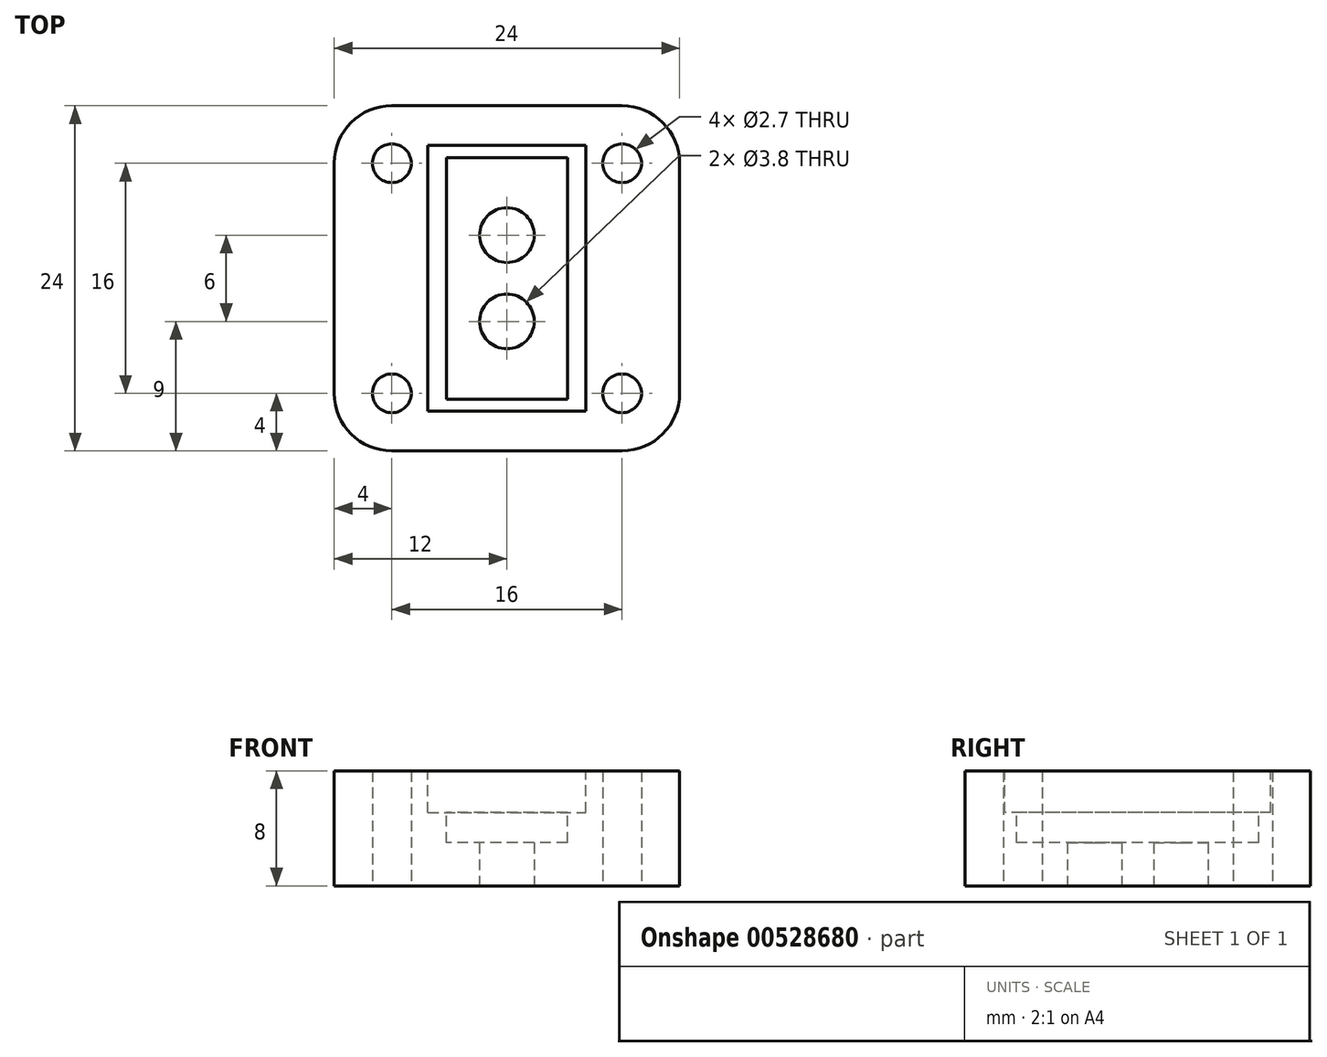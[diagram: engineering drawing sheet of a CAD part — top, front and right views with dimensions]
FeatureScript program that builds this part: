
annotation { "Feature Type Name" : "Feature", "Feature Type Description" : "" }
export const myFeature = defineFeature(function(context is Context, id is Id, definition is map)
    precondition{}
    {
        {
            var Q0;
            Q0=qCreatedBy(makeId("Top.planeOp"),FACE);
            var sketch = newSketch(context, id + "F0", { "sketchPlane" : qUnion([Q0])});
            skLineSegment(sketch, "E0.bottom", {"start": v(12, 12) * mm, "end": v(-12, 12) * mm});
            skLineSegment(sketch, "E0.top", {"start": v(12, -12) * mm, "end": v(-12, -12) * mm});
            skLineSegment(sketch, "E0.left", {"start": v(12, 12) * mm, "end": v(12, -12) * mm});
            skLineSegment(sketch, "E0.right", {"start": v(-12, 12) * mm, "end": v(-12, -12) * mm});
            skPoint(sketch, "E0.middle", {"position": v(0, 0) * mm});
            skLineSegment(sketch, "E1", {"start": v(0, 0) * mm, "end": v(-8, 0) * mm, "construction": true});
            skLineSegment(sketch, "E2", {"start": v(-8, 0) * mm, "end": v(-8, 8) * mm, "construction": true});
            skLineSegment(sketch, "E3", {"start": v(0, 0) * mm, "end": v(0, 3) * mm, "construction": true});
            skCircle(sketch, "E4", {"center": v(-8, 8) * mm, "radius": 1.35 * mm});
            skCircle(sketch, "E5", {"center": v(0, 3) * mm, "radius": 1.9 * mm});
            skCircle(sketch, "E6.0.1.0", {"center": v(-8, -8) * mm, "radius": 1.35 * mm});
            skCircle(sketch, "E6.1.0.0", {"center": v(8, 8) * mm, "radius": 1.35 * mm});
            skCircle(sketch, "E6.1.1.0", {"center": v(8, -8) * mm, "radius": 1.35 * mm});
            skLineSegment(sketch, "E6.direction1", {"start": v(-8, 8) * mm, "end": v(8, 8) * mm, "construction": true});
            skLineSegment(sketch, "E6.direction2", {"start": v(-8, 8) * mm, "end": v(-8, -8) * mm, "construction": true});
            skCircle(sketch, "E7.MirrorC", {"center": v(0, -3) * mm, "radius": 1.9 * mm});
            skSolve(sketch);
        }
        {
            var Q0;
            Q0=makeQuery(id+"F0.imprint","IMPRINT",FACE,{"disambiguationData":[TD([[makeQuery(id+"F0.imprint","IMPRINT",EDGE,{"derivedFrom":sQuery(id+"F0.wireOp",EDGE,"E0.bottom")}),1.0]])]});
            extrude(context, id + "F1", {"entities" : qUnion([Q0]), "depth" : 8 * mm, "offsetDistance" : 25 * mm});
        }
        {
            var Q0;
            Q0=makeQuery(id+"F1.opExtrude","CAP_FACE",FACE,{"disambiguationData":[OSD([sQuery(id+"F0.wireOp",EDGE,"E0.bottom"),sQuery(id+"F0.wireOp",EDGE,"E0.top"),sQuery(id+"F0.wireOp",EDGE,"E0.left"),sQuery(id+"F0.wireOp",EDGE,"E0.right"),sQuery(id+"F0.wireOp",EDGE,"E4"),sQuery(id+"F0.wireOp",EDGE,"E5"),sQuery(id+"F0.wireOp",EDGE,"E6.0.1.0"),sQuery(id+"F0.wireOp",EDGE,"E6.1.0.0"),sQuery(id+"F0.wireOp",EDGE,"E6.1.1.0"),sQuery(id+"F0.wireOp",EDGE,"E7.MirrorC")])],"isStart":false});
            var sketch = newSketch(context, id + "F2", { "sketchPlane" : qUnion([Q0])});
            skLineSegment(sketch, "E8.bottom", {"start": v(4.2, 8.4) * mm, "end": v(-4.2, 8.4) * mm});
            skLineSegment(sketch, "E8.top", {"start": v(4.2, -8.4) * mm, "end": v(-4.2, -8.4) * mm});
            skLineSegment(sketch, "E8.left", {"start": v(4.2, 8.4) * mm, "end": v(4.2, -8.4) * mm});
            skLineSegment(sketch, "E8.right", {"start": v(-4.2, 8.4) * mm, "end": v(-4.2, -8.4) * mm});
            skPoint(sketch, "E8.middle", {"position": v(0, 0) * mm});
            skLineSegment(sketch, "E9", {"start": v(-8, 8) * mm, "end": v(-8, 0) * mm, "construction": true});
            skCircle(sketch, "E10", {"center": v(0, 0) * mm, "radius": 8 * mm, "construction": true});
            skLineSegment(sketch, "E11.bottom", {"start": v(-9.25, 9.25) * mm, "end": v(9.25, 9.25) * mm, "construction": true});
            skLineSegment(sketch, "E11.top", {"start": v(-9.25, -9.25) * mm, "end": v(9.25, -9.25) * mm, "construction": true});
            skLineSegment(sketch, "E11.left", {"start": v(-9.25, 9.25) * mm, "end": v(-9.25, -9.25) * mm, "construction": true});
            skLineSegment(sketch, "E11.right", {"start": v(9.25, 9.25) * mm, "end": v(9.25, -9.25) * mm, "construction": true});
            skLineSegment(sketch, "E12.bottom", {"start": v(-5.5, 9.25) * mm, "end": v(5.5, 9.25) * mm});
            skLineSegment(sketch, "E12.top", {"start": v(-5.5, -9.25) * mm, "end": v(5.5, -9.25) * mm});
            skLineSegment(sketch, "E12.left", {"start": v(-5.5, 9.25) * mm, "end": v(-5.5, -9.25) * mm});
            skLineSegment(sketch, "E12.right", {"start": v(5.5, 9.25) * mm, "end": v(5.5, -9.25) * mm});
            skSolve(sketch);
        }
        {
            var Q0;
            Q0=makeQuery(id+"F2.imprint","IMPRINT",FACE,{"disambiguationData":[TD([[makeQuery(id+"F2.imprint","IMPRINT",EDGE,{"derivedFrom":sQuery(id+"F2.wireOp",EDGE,"E8.bottom")}),1.0]])]});
            extrude(context, id + "F3", {"entities" : qUnion([Q0]), "operationType" : NewBodyOperationType.REMOVE, "oppositeDirection" : true, "depth" : 5 * mm, "offsetDistance" : 25 * mm});
        }
        {
            var Q0;
            Q0 = qSketchRegion(id + "F2", true);
            extrude(context, id + "F4", {"entities" : qUnion([Q0]), "operationType" : NewBodyOperationType.REMOVE, "oppositeDirection" : true, "depth" : 2.9 * mm, "offsetDistance" : 25 * mm});
        }
        {
            var Q0;
            Q0=makeQuery(id+"F1.opExtrude","SWEPT_EDGE",EDGE,{"disambiguationData":[OSD([sQuery(id+"F0.wireOp",EDGE,"E0.bottom"),sQuery(id+"F0.wireOp",EDGE,"E0.right")])]});
            var Q1;
            Q1=makeQuery(id+"F1.opExtrude","SWEPT_EDGE",EDGE,{"disambiguationData":[OSD([sQuery(id+"F0.wireOp",EDGE,"E0.bottom"),sQuery(id+"F0.wireOp",EDGE,"E0.left")])]});
            var Q2;
            Q2=makeQuery(id+"F1.opExtrude","SWEPT_EDGE",EDGE,{"disambiguationData":[OSD([sQuery(id+"F0.wireOp",EDGE,"E0.top"),sQuery(id+"F0.wireOp",EDGE,"E0.left")])]});
            var Q3;
            Q3=makeQuery(id+"F1.opExtrude","SWEPT_EDGE",EDGE,{"disambiguationData":[OSD([sQuery(id+"F0.wireOp",EDGE,"E0.top"),sQuery(id+"F0.wireOp",EDGE,"E0.right")])]});
            fillet(context, id + "F5", {"entities" : qUnion([Q0, Q1, Q2, Q3]), "tangentPropagation" : true, "radius" : 4 * mm, "defaultsChanged" : true, "vertexSettings" : [], "allowEdgeOverflow" : false});
        }
    });
